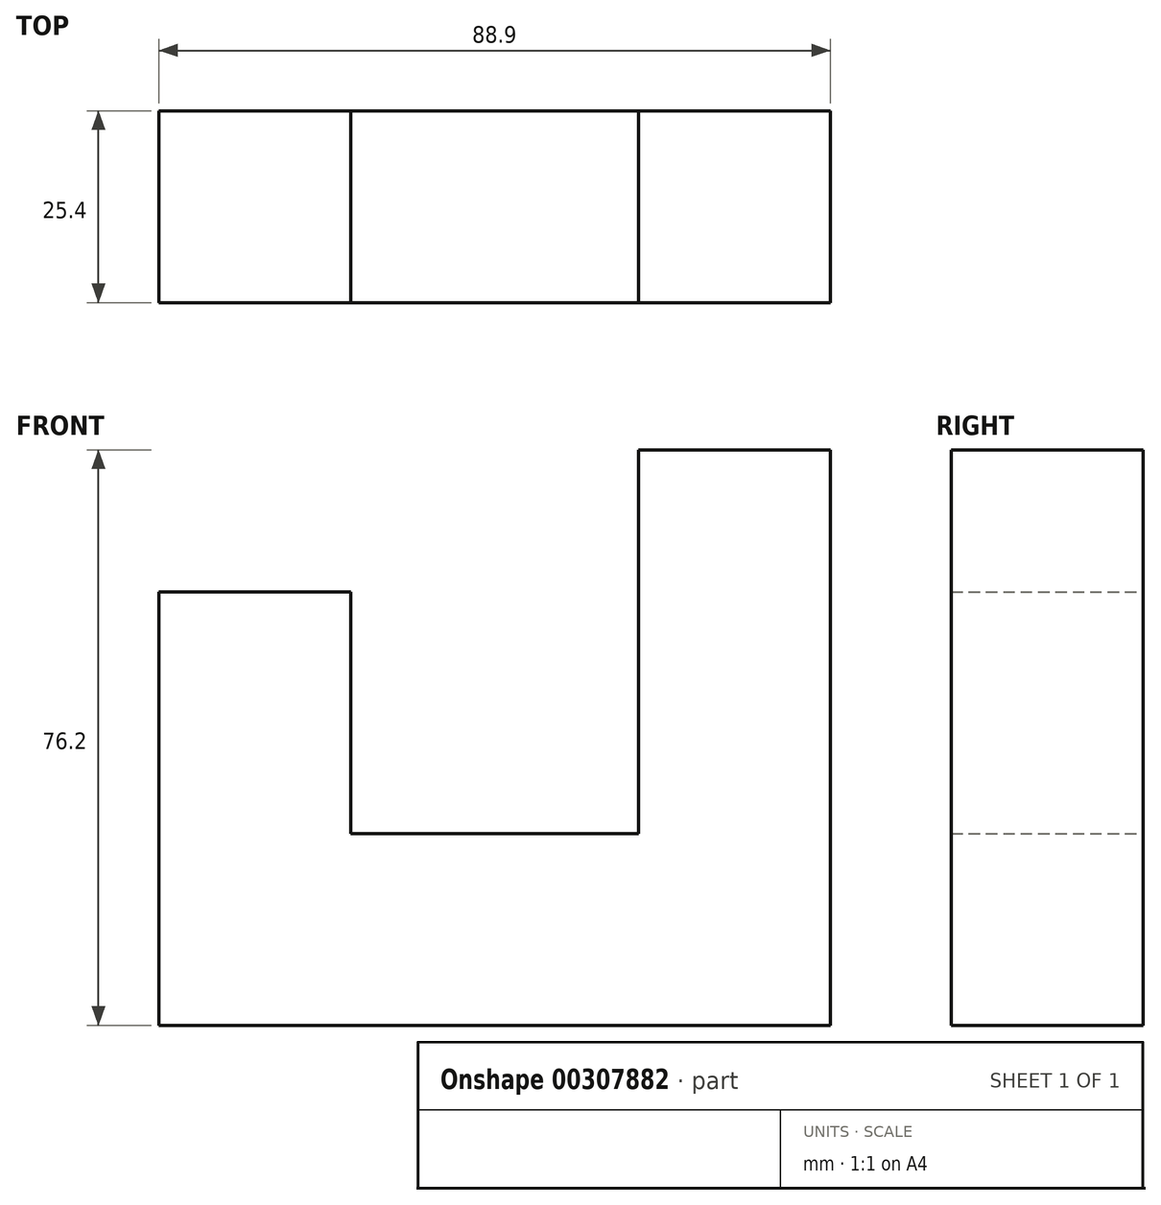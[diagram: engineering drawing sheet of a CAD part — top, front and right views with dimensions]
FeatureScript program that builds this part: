
annotation { "Feature Type Name" : "Feature", "Feature Type Description" : "" }
export const myFeature = defineFeature(function(context is Context, id is Id, definition is map)
    precondition{}
    {
        {
            var Q0;
            Q0=qCreatedBy(makeId("Front.planeOp"),FACE);
            var sketch = newSketch(context, id + "F0", { "sketchPlane" : qUnion([Q0])});
            skLineSegment(sketch, "E0", {"start": v(-43.68, -35.89) * mm, "end": v(45.22, -35.89) * mm});
            skLineSegment(sketch, "E1", {"start": v(45.22, -35.89) * mm, "end": v(45.22, 40.31) * mm});
            skLineSegment(sketch, "E2", {"start": v(45.22, 40.31) * mm, "end": v(19.82, 40.31) * mm});
            skLineSegment(sketch, "E3", {"start": v(19.82, 40.31) * mm, "end": v(19.82, -10.49) * mm});
            skLineSegment(sketch, "E4", {"start": v(19.82, -10.49) * mm, "end": v(-18.28, -10.49) * mm});
            skLineSegment(sketch, "E5", {"start": v(-18.28, -10.49) * mm, "end": v(-18.28, 21.51) * mm});
            skLineSegment(sketch, "E6", {"start": v(-18.28, 21.51) * mm, "end": v(-43.68, 21.51) * mm});
            skLineSegment(sketch, "E7", {"start": v(-43.68, 21.51) * mm, "end": v(-43.68, -35.89) * mm});
            skSolve(sketch);
        }
        {
            var Q0;
            Q0=makeQuery(id+"F0.imprint","IMPRINT",FACE,{"disambiguationData":[TD([[makeQuery(id+"F0.imprint","IMPRINT",EDGE,{"derivedFrom":sQuery(id+"F0.wireOp",EDGE,"E0")}),1.0]])]});
            extrude(context, id + "F1", {"entities" : qUnion([Q0]), "depth" : 25.4 * mm});
        }
    });
